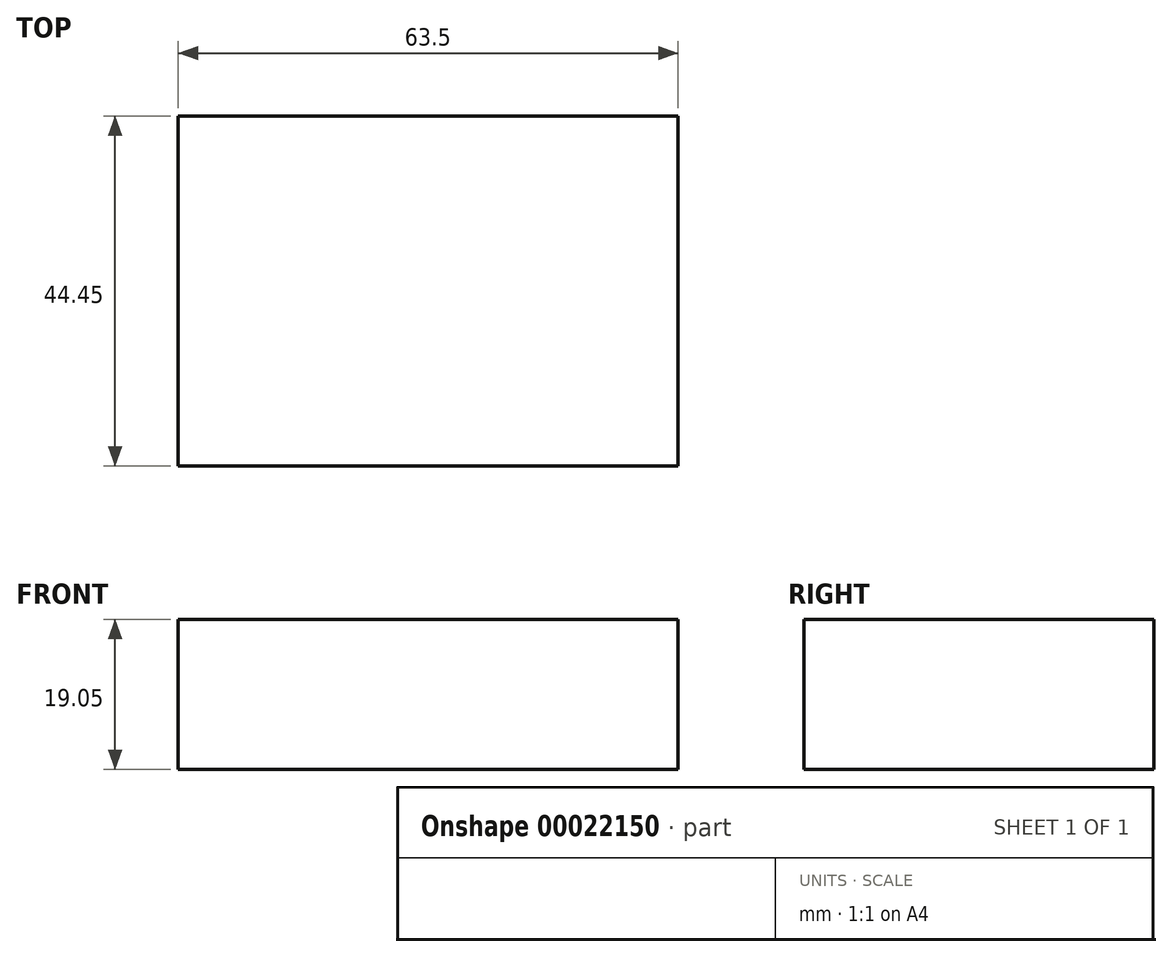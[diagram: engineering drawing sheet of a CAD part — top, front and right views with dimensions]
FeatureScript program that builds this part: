
annotation { "Feature Type Name" : "Feature", "Feature Type Description" : "" }
export const myFeature = defineFeature(function(context is Context, id is Id, definition is map)
    precondition{}
    {
        {
            var Q0;
            Q0=qCreatedBy(makeId("Top.planeOp"),FACE);
            var sketch = newSketch(context, id + "F0", { "sketchPlane" : qUnion([Q0])});
            skLineSegment(sketch, "E0.bottom", {"start": v(-97.8, 7.57) * mm, "end": v(-34.3, 7.57) * mm});
            skLineSegment(sketch, "E0.top", {"start": v(-97.8, -36.88) * mm, "end": v(-34.3, -36.88) * mm});
            skLineSegment(sketch, "E0.left", {"start": v(-97.8, 7.57) * mm, "end": v(-97.8, -36.88) * mm});
            skLineSegment(sketch, "E0.right", {"start": v(-34.3, 7.57) * mm, "end": v(-34.3, -36.88) * mm});
            skSolve(sketch);
        }
        {
            var Q0;
            Q0 = qSketchRegion(id + "F0", true);
            extrude(context, id + "F1", {"entities" : qUnion([Q0]), "depth" : 19.05 * mm});
        }
    });
